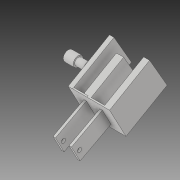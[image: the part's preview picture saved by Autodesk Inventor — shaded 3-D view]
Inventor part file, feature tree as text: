
AUTODESK INVENTOR PART (.ipt)
format: ipt  version: 2017 (Build 210142000, 142)  size: 413,184 bytes
history: native  units: mm
features: sketch x34, extrude x28, thicken_offset x26, plane x6, projected_geometry x2, mirror x1
ambient origin geometry x8: Origin, YZ Plane, XZ Plane, XY Plane, X Axis, Y Axis, Z Axis, Center Point
bodies: Solid1 (feature_tree)
feature tree (97):
  extrude  "Extrusion1"  Depth=10.0mm TaperAngle=0.0deg
  thicken_offset  "Thicken1"
  thicken_offset  "Thicken2"
  thicken_offset  "Thicken3"
  thicken_offset  "Thicken4"
  extrude  "Extrusion2"  Depth=5.0mm
  extrude  "Extrusion3"  Depth=5.0mm
  thicken_offset  "Thicken5"
  extrude  "Extrusion4"  Depth=200.0mm
  thicken_offset  "Thicken6"
  thicken_offset  "Thicken7"
  plane  "Work Plane1"
  extrude  "Extrusion6"  Depth=30.0mm
  thicken_offset  "Thicken8"
  thicken_offset  "Thicken9"
  thicken_offset  "Thicken10"
  extrude  "Extrusion7"  Depth=40.0mm TaperAngle=0.0deg
  thicken_offset  "Thicken12"
  extrude  "Extrusion8"  Depth=100.0mm
  extrude  "Extrusion9"  Depth=40.0mm
  thicken_offset  "Thicken13"
  thicken_offset  "Thicken14"
  extrude  "Extrusion10"  Depth=5.0mm
  sketch  "Sketch11"  dims[d25=5.0mm d26=-40.0mm]
  extrude  "Extrusion11"  [1 undecoded]
  thicken_offset  "Thicken15"
  thicken_offset  "Thicken16"
  thicken_offset  "Thicken17"
  thicken_offset  "Thicken18"
  plane  "Work Plane2"
  extrude  "Extrusion12"  Depth=40.0mm
  thicken_offset  "Thicken19"
  thicken_offset  "Thicken20"
  extrude  "Extrusion13"  Depth=20.0mm
  thicken_offset  "Thicken21"
  extrude  "Extrusion14"  Depth=20.0mm
  sketch  "Sketch16"  dims[d39=65.0mm d40=65.0mm]
  plane  "Work Plane3"
  extrude  "Extrusion15"  Depth=20.0mm TaperAngle=0.0deg
  sketch  "Sketch18"  dims[d45=15.0mm d46=15.0mm]
  plane  "Work Plane4"
  extrude  "Extrusion16"  Depth=65.0mm
  thicken_offset  "Thicken22"
  thicken_offset  "Thicken23"
  thicken_offset  "Thicken24"
  thicken_offset  "Thicken25"
  extrude  "Extrusion17"  Depth=70.0mm TaperAngle=0.0deg
  extrude  "Extrusion18"  Depth=15.0mm
  thicken_offset  "Thicken26"
  thicken_offset  "Thicken27"
  sketch  "Sketch22"  dims[d55=2.0mm d56=2.0mm]
  extrude  "Extrusion19"  Depth=7.0mm
  sketch  "Sketch24"  dims[d59=4.0mm d60=2.0mm]
  plane  "Work Plane5"
  extrude  "Extrusion20"  Depth=70.0mm TaperAngle=0.0deg
  extrude  "Extrusion21"  Depth=70.0mm
  extrude  "Extrusion22"  Depth=2.0mm
  sketch  "Sketch28"  dims[d68=20.0mm d69=70.0mm d70=0.0mm]
  extrude  "Extrusion23"  Depth=4.0mm
  extrude  "Extrusion24"  Depth=2.0mm
  extrude  "Extrusion25"  [1 undecoded]
  extrude  "Extrusion26"  Depth=150.0mm
  extrude  "Extrusion27"  Depth=20.0mm
  extrude  "Extrusion28"  Depth=70.0mm TaperAngle=0.0deg
  plane  "Work Plane6"
  mirror  "Mirror1"
  extrude  "Extrusion29"  Depth=30.0mm
  sketch  "Sketch1"  dims[d1=18.0mm d2=10.0mm d3=0.0mm]
  sketch  "Sketch2"  dims[d4=5.0mm d5=5.0mm]
  sketch  "Sketch3"  dims[d6=5.0mm d7=5.0mm]
  sketch  "Sketch4"  dims[d8=200.0mm d9=200.0mm]
  sketch  "Sketch6"  dims[d10=30.0mm d11=30.0mm]
  sketch  "Sketch7"  dims[d12=100.0mm d13=0.0mm d14=40.0mm d15=0.0mm]
  sketch  "Sketch8"  dims[d16=100.0mm d17=100.0mm]
  sketch  "Sketch9"  dims[d18=40.0mm d19=0.0mm d20=40.0mm]
  sketch  "Sketch10"  dims[d21=40.0mm d24=5.0mm]
  sketch  "Sketch12"  dims[d27=40.0mm d28=0.0mm d29=100.0mm]
  sketch  "Sketch13"  dims[d30=100.0mm d31=20.0mm]
  sketch  "Sketch14"  dims[d32=20.0mm d33=20.0mm]
  sketch  "Sketch15"  dims[d34=20.0mm d35=400.0mm d36=0.0mm]
  sketch  "Sketch17"  dims[d41=300.0mm d42=0.0mm d43=70.0mm d44=0.0mm]
  sketch  "Sketch19"  dims[d47=7.0mm d48=7.0mm]
  sketch  "Sketch20"  dims[d49=35.0mm d50=70.0mm d51=0.0mm]
  projected_geometry  "Projected Loop1"
  sketch  "Sketch21"  dims[d52=70.0mm d53=0.0mm d54=2.0mm]
  sketch  "Sketch23"  dims[d57=2.0mm d58=4.0mm]
  sketch  "Sketch25"  dims[d61=2.0mm d62=-167.5mm]
  sketch  "Sketch26"  dims[d63=30.0mm d64=0.0mm d65=150.0mm]
  sketch  "Sketch27"  dims[d66=150.0mm d67=20.0mm]
  sketch  "Sketch29"  dims[d71=30.0mm d72=30.0mm]
  sketch  "Sketch30"  dims[d73=30.0mm d74=0.0mm]
  projected_geometry  "Projected Loop2"
  sketch  "Sketch31"  dims[d75=-15.0mm]
  sketch  "Sketch32"  dims[d76=14.0mm d77=0.0mm]
  sketch  "Sketch33"  dims[d78=-2.0mm]
  sketch  "Sketch34"  dims[d79=14.0mm d80=0.0mm]
  sketch  "Sketch35"  dims[d81=150.0mm d82=150.0mm d83=150.0mm d84=150.0mm d85=150.0mm d86=150.0mm d87=150.0mm d88=150.0mm d89=40.0mm d90=0.0mm d91=40.0mm d92=0.0mm d93=3.0mm d94=3.0mm d95=3.0mm d96=3.0mm d97=50.0mm d98=0.0mm d99=-2.0mm d100=31.0mm d101=0.0mm d102=1000.0mm d103=0.0mm d104=10.0mm d105=0.0mm d106=70.0mm d107=0.0mm d108=70.0mm d109=0.0mm d110=70.0mm d111=0.0mm d112=20.0mm d113=0.0mm d114=20.0mm d115=0.0mm d116=20.0mm d117=0.0mm d118=-41.527mm d119=60.0mm d120=0.0mm]
note: 2 required parameter values undecoded (feature->parameter linkage not recoverable at this tier; creation-order binding heuristic only, values carry confidence <= 0.55)
